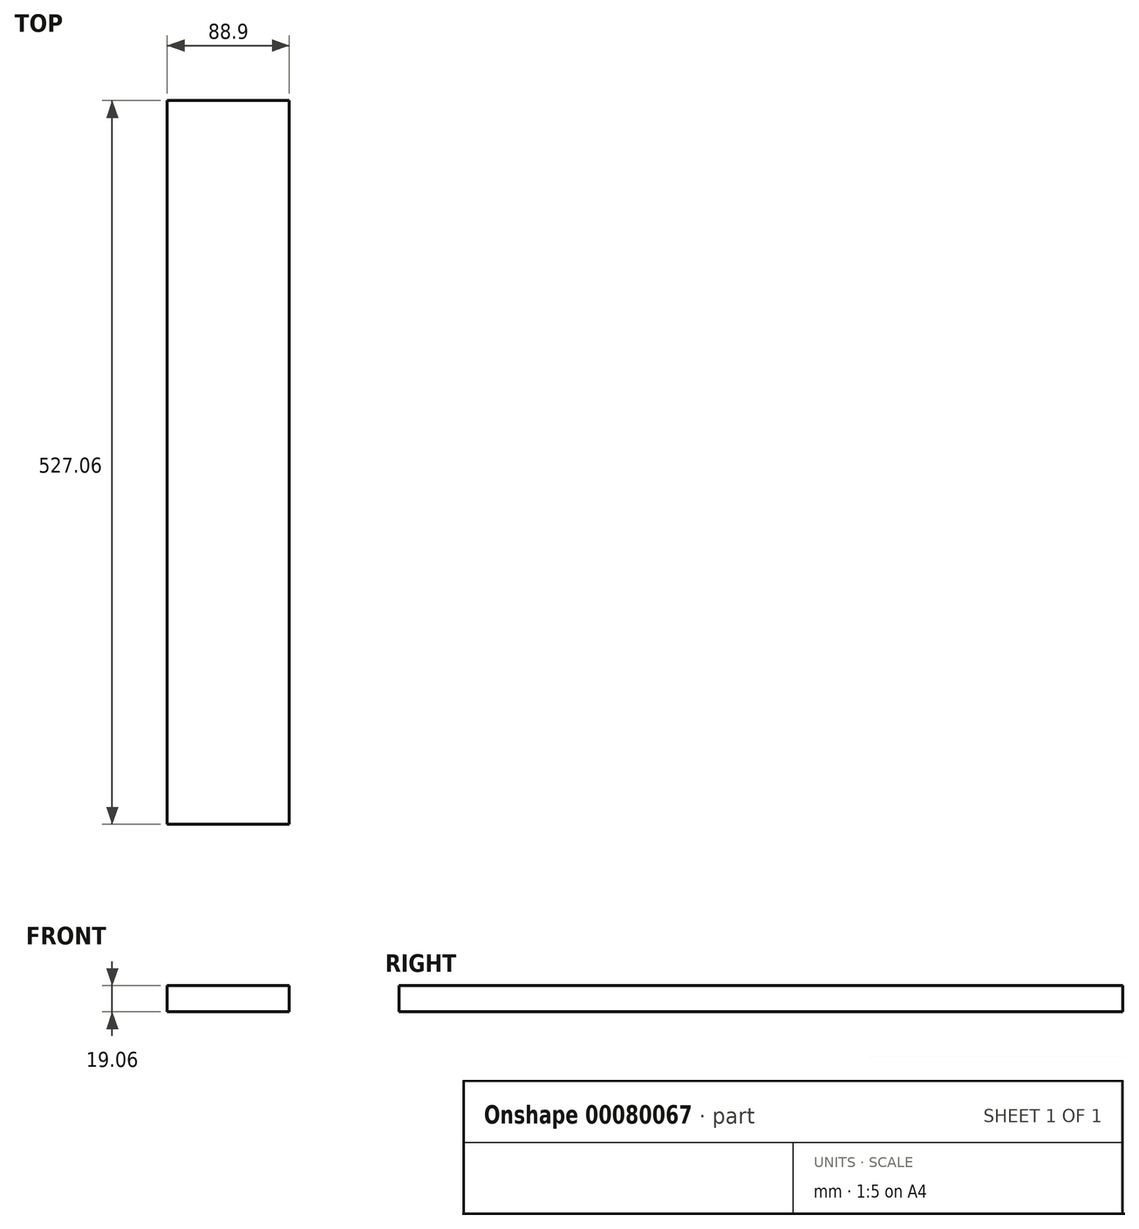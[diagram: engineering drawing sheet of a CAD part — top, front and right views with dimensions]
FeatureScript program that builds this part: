
annotation { "Feature Type Name" : "Feature", "Feature Type Description" : "" }
export const myFeature = defineFeature(function(context is Context, id is Id, definition is map)
    precondition{}
    {
        {
            var Q0;
            Q0=qCreatedBy(makeId("Front.planeOp"),FACE);
            var sketch = newSketch(context, id + "F0", { "sketchPlane" : qUnion([Q0])});
            skLineSegment(sketch, "E0.bottom", {"start": v(-44.45, 9.52) * mm, "end": v(44.45, 9.52) * mm});
            skLineSegment(sketch, "E0.top", {"start": v(-44.45, -9.52) * mm, "end": v(44.45, -9.52) * mm});
            skLineSegment(sketch, "E0.left", {"start": v(-44.45, 9.52) * mm, "end": v(-44.45, -9.52) * mm});
            skLineSegment(sketch, "E0.right", {"start": v(44.45, 9.52) * mm, "end": v(44.45, -9.52) * mm});
            skPoint(sketch, "E0.middle", {"position": v(0, 0) * mm});
            skSolve(sketch);
        }
        {
            var Q0;
            Q0 = qSketchRegion(id + "F0", true);
            extrude(context, id + "F1", {"entities" : qUnion([Q0]), "endBound" : BoundingType.SYMMETRIC, "depth" : 527.05 * mm});
        }
    });
